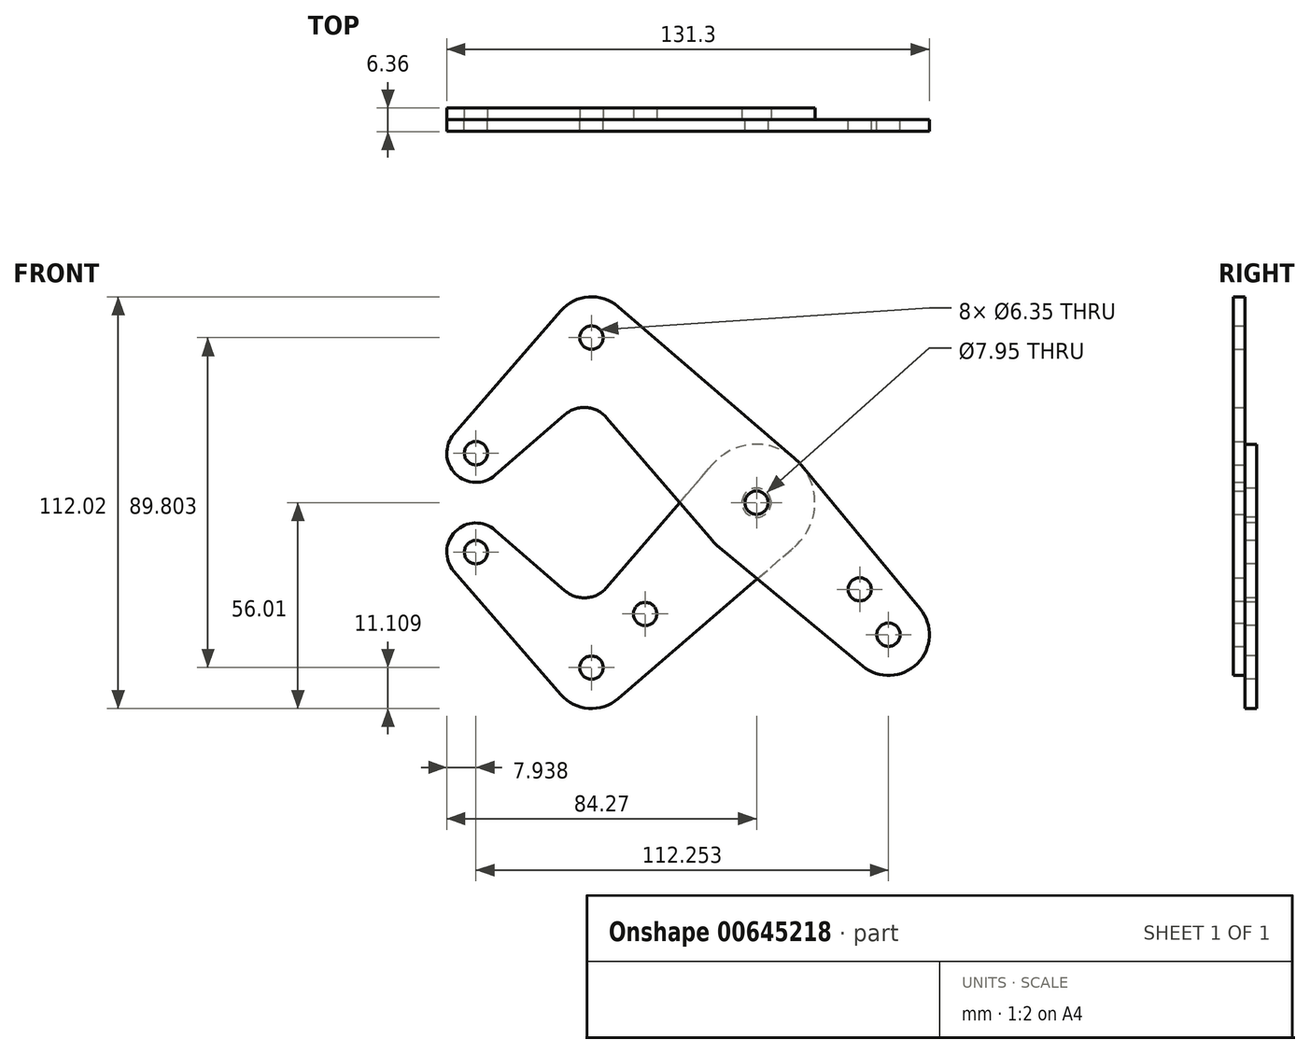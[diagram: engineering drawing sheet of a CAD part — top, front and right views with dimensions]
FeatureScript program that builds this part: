
annotation { "Feature Type Name" : "Feature", "Feature Type Description" : "" }
export const myFeature = defineFeature(function(context is Context, id is Id, definition is map)
    precondition{}
    {
        {
            var Q0;
            Q0=qCreatedBy(makeId("Front.planeOp"),FACE);
            var sketch = newSketch(context, id + "F0", { "sketchPlane" : qUnion([Q0])});
            skCircle(sketch, "E0", {"center": v(-76.33, 13.47) * mm, "radius": 7.94 * mm});
            skCircle(sketch, "E1", {"center": v(-44.9, 44.9) * mm, "radius": 11.11 * mm});
            skLineSegment(sketch, "E2", {"start": v(-44.9, 44.9) * mm, "end": v(35.92, -35.92) * mm, "construction": true});
            skCircle(sketch, "E3", {"center": v(0, 0) * mm, "radius": 15.88 * mm});
            skCircle(sketch, "E4", {"center": v(35.92, -35.92) * mm, "radius": 11.11 * mm});
            skCircle(sketch, "E5", {"center": v(-76.33, 13.47) * mm, "radius": 3.18 * mm});
            skCircle(sketch, "E6", {"center": v(-44.9, 44.9) * mm, "radius": 3.18 * mm});
            skCircle(sketch, "E7", {"center": v(0, 0) * mm, "radius": 3.98 * mm});
            skCircle(sketch, "E8", {"center": v(35.92, -35.92) * mm, "radius": 3.18 * mm});
            skCircle(sketch, "E9", {"center": v(28.07, -23.58) * mm, "radius": 3.18 * mm});
            skLineSegment(sketch, "E10", {"start": v(28.07, -23.58) * mm, "end": v(25.83, -25.83) * mm});
            skLineSegment(sketch, "E11", {"start": v(-82.33, 18.67) * mm, "end": v(-53.3, 52.18) * mm});
            skLineSegment(sketch, "E12", {"start": v(-52.08, 23.98) * mm, "end": v(-71.13, 7.47) * mm});
            skLineSegment(sketch, "E13", {"start": v(28.83, -44.48) * mm, "end": v(-10.12, -12.23) * mm});
            skLineSegment(sketch, "E14", {"start": v(44.48, -28.83) * mm, "end": v(12.23, 10.12) * mm});
            skLineSegment(sketch, "E15", {"start": v(-40.85, 23.15) * mm, "end": v(-12.04, -10.35) * mm});
            skLineSegment(sketch, "E16", {"start": v(-37.66, 53.33) * mm, "end": v(10.35, 12.04) * mm});
            skArc(sketch, "E17", {"start": v(-40.85, 23.15) * mm, "mid": v(-46.3, 25.9) * mm, "end": v(-52.08, 23.98) * mm});
            skCircle(sketch, "E18", {"center": v(-30.3, -30.3) * mm, "radius": 3.18 * mm});
            skCircle(sketch, "E19", {"center": v(-44.9, -44.9) * mm, "radius": 11.11 * mm});
            skLineSegment(sketch, "E20", {"start": v(-44.9, -44.9) * mm, "end": v(-76.33, -13.47) * mm, "construction": true});
            skCircle(sketch, "E21", {"center": v(-76.33, -13.47) * mm, "radius": 7.94 * mm});
            skCircle(sketch, "E22", {"center": v(-76.33, -13.47) * mm, "radius": 3.18 * mm});
            skLineSegment(sketch, "E23", {"start": v(-76.33, -13.47) * mm, "end": v(-74.09, -15.72) * mm});
            skLineSegment(sketch, "E24", {"start": v(-82.33, -18.67) * mm, "end": v(-53.3, -52.18) * mm});
            skLineSegment(sketch, "E25", {"start": v(-71.13, -7.47) * mm, "end": v(-52.08, -23.98) * mm});
            skLineSegment(sketch, "E26", {"start": v(-53.33, -37.66) * mm, "end": v(-52.78, -37.02) * mm});
            skLineSegment(sketch, "E27", {"start": v(-37.66, -53.33) * mm, "end": v(10.35, -12.04) * mm});
            skArc(sketch, "E28", {"start": v(-52.08, -23.98) * mm, "mid": v(-46.3, -25.9) * mm, "end": v(-40.85, -23.15) * mm});
            skLineSegment(sketch, "E29.trimOffspring", {"start": v(-40.85, -23.15) * mm, "end": v(-12.04, 10.35) * mm});
            skLineSegment(sketch, "E30", {"start": v(-44.9, 44.9) * mm, "end": v(-76.33, 13.47) * mm, "construction": true});
            skCircle(sketch, "E31", {"center": v(0, 0) * mm, "radius": 3.18 * mm});
            skLineSegment(sketch, "E32", {"start": v(-44.9, -44.9) * mm, "end": v(0, 0) * mm, "construction": true});
            skLineSegment(sketch, "E33", {"start": v(-76.33, 13.47) * mm, "end": v(-76.33, -13.47) * mm, "construction": true});
            skCircle(sketch, "E34", {"center": v(-44.9, -44.9) * mm, "radius": 3.18 * mm});
            skSolve(sketch);
        }
        {
            var Q0;
            {var subQ0=sQuery(id+"F0.wireOp",EDGE,"E11");Q0=makeQuery(id+"F0.imprint","IMPRINT",FACE,{"disambiguationData":[TD([[makeQuery(id+"F0.imprint","IMPRINT",EDGE,{"derivedFrom":subQ0}),-1.0]])]});}
            var Q1;
            Q1=makeQuery(id+"F0.imprint","IMPRINT",FACE,{"disambiguationData":[TD([[makeQuery(id+"F0.imprint","IMPRINT",EDGE,{"derivedFrom":sQuery(id+"F0.wireOp",EDGE,"E5")}),-1.0]])]});
            var Q2;
            Q2=makeQuery(id+"F0.imprint","IMPRINT",FACE,{"disambiguationData":[TD([[makeQuery(id+"F0.imprint","IMPRINT",EDGE,{"derivedFrom":sQuery(id+"F0.wireOp",EDGE,"E6")}),-1.0]])]});
            var Q3;
            Q3=makeQuery(id+"F0.imprint","IMPRINT",FACE,{"disambiguationData":[TD([[makeQuery(id+"F0.imprint","IMPRINT",EDGE,{"derivedFrom":sQuery(id+"F0.wireOp",EDGE,"E7")}),-1.0]])]});
            var Q4;
            Q4=makeQuery(id+"F0.imprint","IMPRINT",FACE,{"disambiguationData":[TD([[makeQuery(id+"F0.imprint","IMPRINT",EDGE,{"derivedFrom":sQuery(id+"F0.wireOp",EDGE,"E7")}),1.0]])]});
            var Q5;
            Q5=makeQuery(id+"F0.imprint","IMPRINT",FACE,{"disambiguationData":[TD([[makeQuery(id+"F0.imprint","IMPRINT",EDGE,{"derivedFrom":sQuery(id+"F0.wireOp",EDGE,"E9")}),-1.0]])]});
            var Q6;
            Q6=makeQuery(id+"F0.imprint","IMPRINT",FACE,{"disambiguationData":[TD([[makeQuery(id+"F0.imprint","IMPRINT",EDGE,{"derivedFrom":sQuery(id+"F0.wireOp",EDGE,"E8")}),-1.0]])]});
            var Q7;
            {var subQ0=sQuery(id+"F0.wireOp",EDGE,"E13");var subQ1=sQuery(id+"F0.wireOp",EDGE,"E3");var subQ2=makeQuery(id+"F0.imprint","INTERSECT",VERTEX,{"derivedFrom":[subQ1,subQ0]});Q7=makeQuery(id+"F0.imprint","IMPRINT",FACE,{"disambiguationData":[TD([[makeQuery(id+"F0.imprint","IMPRINT",EDGE,{"disambiguationData":[TD([[subQ2,-1.0]])],"derivedFrom":subQ1}),-1.0]])]});}
            var Q8;
            {var subQ0=sQuery(id+"F0.wireOp",EDGE,"E15");var subQ1=sQuery(id+"F0.wireOp",EDGE,"E3");var subQ2=makeQuery(id+"F0.imprint","INTERSECT",VERTEX,{"derivedFrom":[subQ1,subQ0]});Q8=makeQuery(id+"F0.imprint","IMPRINT",FACE,{"disambiguationData":[TD([[makeQuery(id+"F0.imprint","IMPRINT",EDGE,{"disambiguationData":[TD([[subQ2,1.0]])],"derivedFrom":subQ1}),-1.0]])]});}
            extrude(context, id + "F1", {"entities" : qUnion([Q0, Q1, Q2, Q3, Q4, Q5, Q6, Q7, Q8]), "depth" : 3.17 * mm, "offsetDistance" : 25.4 * mm});
        }
        {
            var Q0;
            Q0=makeQuery(id+"F0.imprint","IMPRINT",FACE,{"disambiguationData":[TD([[makeQuery(id+"F0.imprint","IMPRINT",EDGE,{"derivedFrom":sQuery(id+"F0.wireOp",EDGE,"E18")}),-1.0]])]});
            var Q1;
            {var subQ0=sQuery(id+"F0.wireOp",EDGE,"E13");var subQ1=sQuery(id+"F0.wireOp",EDGE,"E3");var subQ2=makeQuery(id+"F0.imprint","INTERSECT",VERTEX,{"derivedFrom":[subQ1,subQ0]});Q1=makeQuery(id+"F0.imprint","IMPRINT",FACE,{"disambiguationData":[TD([[makeQuery(id+"F0.imprint","IMPRINT",EDGE,{"disambiguationData":[TD([[subQ2,-1.0]])],"derivedFrom":subQ1}),-1.0]])]});}
            var Q2;
            {var subQ0=sQuery(id+"F0.wireOp",EDGE,"E15");var subQ1=sQuery(id+"F0.wireOp",EDGE,"E3");var subQ2=makeQuery(id+"F0.imprint","INTERSECT",VERTEX,{"derivedFrom":[subQ1,subQ0]});Q2=makeQuery(id+"F0.imprint","IMPRINT",FACE,{"disambiguationData":[TD([[makeQuery(id+"F0.imprint","IMPRINT",EDGE,{"disambiguationData":[TD([[subQ2,1.0]])],"derivedFrom":subQ1}),-1.0]])]});}
            var Q3;
            Q3=makeQuery(id+"F0.imprint","IMPRINT",FACE,{"disambiguationData":[TD([[makeQuery(id+"F0.imprint","IMPRINT",EDGE,{"derivedFrom":sQuery(id+"F0.wireOp",EDGE,"E7")}),-1.0]])]});
            var Q4;
            Q4=makeQuery(id+"F0.imprint","IMPRINT",FACE,{"disambiguationData":[TD([[makeQuery(id+"F0.imprint","IMPRINT",EDGE,{"derivedFrom":sQuery(id+"F0.wireOp",EDGE,"E34")}),-1.0]])]});
            var Q5;
            Q5=makeQuery(id+"F0.imprint","IMPRINT",FACE,{"disambiguationData":[TD([[makeQuery(id+"F0.imprint","IMPRINT",EDGE,{"derivedFrom":sQuery(id+"F0.wireOp",EDGE,"E22")}),-1.0]])]});
            extrude(context, id + "F2", {"entities" : qUnion([Q0, Q1, Q2, Q3, Q4, Q5]), "oppositeDirection" : true, "depth" : 3.17 * mm, "offsetDistance" : 25.4 * mm});
        }
        {
            var Q0;
            Q0=makeQuery(id+"F1.opExtrude","CAP_FACE",FACE,{"disambiguationData":[OSD([sQuery(id+"F0.wireOp",EDGE,"E0"),sQuery(id+"F0.wireOp",EDGE,"E1"),sQuery(id+"F0.wireOp",EDGE,"E3"),sQuery(id+"F0.wireOp",EDGE,"E4"),sQuery(id+"F0.wireOp",EDGE,"E5"),sQuery(id+"F0.wireOp",EDGE,"E6"),sQuery(id+"F0.wireOp",EDGE,"E8"),sQuery(id+"F0.wireOp",EDGE,"E9"),sQuery(id+"F0.wireOp",EDGE,"E11"),sQuery(id+"F0.wireOp",EDGE,"E12"),sQuery(id+"F0.wireOp",EDGE,"E13"),sQuery(id+"F0.wireOp",EDGE,"E14"),sQuery(id+"F0.wireOp",EDGE,"E15"),sQuery(id+"F0.wireOp",EDGE,"E16"),sQuery(id+"F0.wireOp",EDGE,"E17"),sQuery(id+"F0.wireOp",EDGE,"E31")])],"isStart":false});
            var sketch = newSketch(context, id + "F3", { "sketchPlane" : qUnion([Q0])});
            skCircle(sketch, "E35", {"center": v(-44.9, 44.9) * mm, "radius": 3.98 * mm});
            skCircle(sketch, "E36", {"center": v(0, 0) * mm, "radius": 3.98 * mm});
            skCircle(sketch, "E37", {"center": v(35.92, -35.92) * mm, "radius": 11.11 * mm});
            skSolve(sketch);
        }
    });
